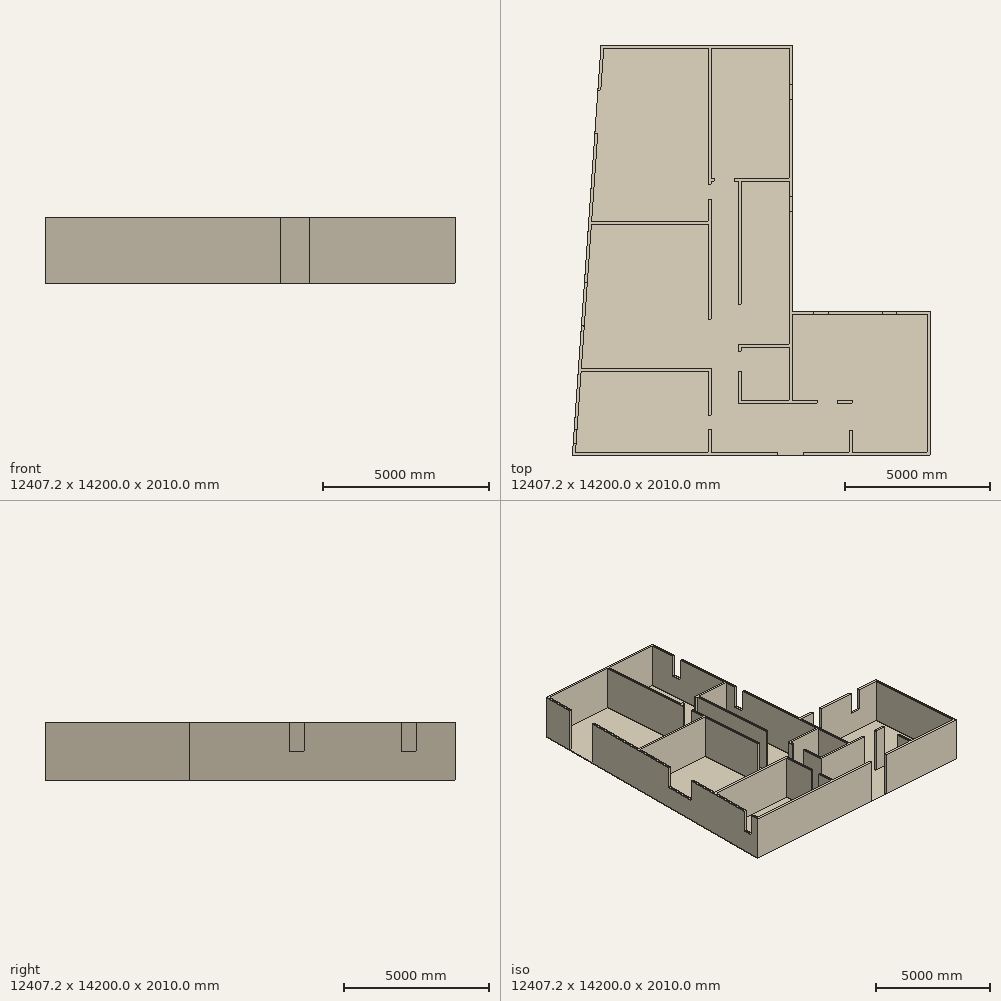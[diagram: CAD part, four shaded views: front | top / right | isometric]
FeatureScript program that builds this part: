
annotation { "Feature Type Name" : "Feature", "Feature Type Description" : "" }
export const myFeature = defineFeature(function(context is Context, id is Id, definition is map)
    precondition{}
    {
        {
            var Q0;
            Q0=qCreatedBy(makeId("Top.planeOp"),FACE);
            var sketch = newSketch(context, id + "F0", { "sketchPlane" : qUnion([Q0])});
            skLineSegment(sketch, "E0.bottom", {"start": v(0, 0) * mm, "end": v(20000, 0) * mm, "construction": true});
            skLineSegment(sketch, "E0.top", {"start": v(0, 20000) * mm, "end": v(20000, 20000) * mm, "construction": true});
            skLineSegment(sketch, "E0.left", {"start": v(0, 0) * mm, "end": v(0, 20000) * mm, "construction": true});
            skLineSegment(sketch, "E0.right", {"start": v(20000, 0) * mm, "end": v(20000, 20000) * mm, "construction": true});
            skLineSegment(sketch, "E1.bottom", {"start": v(0, 0) * mm, "end": v(100, 0) * mm, "construction": true});
            skLineSegment(sketch, "E1.top", {"start": v(0, 100) * mm, "end": v(100, 100) * mm, "construction": true});
            skLineSegment(sketch, "E1.left", {"start": v(0, 0) * mm, "end": v(0, 100) * mm, "construction": true});
            skLineSegment(sketch, "E1.right", {"start": v(100, 0) * mm, "end": v(100, 100) * mm, "construction": true});
            skLineSegment(sketch, "E2", {"start": v(100, 100) * mm, "end": v(1078.98, 14100) * mm});
            skLineSegment(sketch, "E3", {"start": v(100, 100) * mm, "end": v(12300, 100) * mm});
            skLineSegment(sketch, "E4", {"start": v(12300, 100) * mm, "end": v(12300, 4900) * mm});
            skLineSegment(sketch, "E5", {"start": v(7500, 4900) * mm, "end": v(7500, 14100) * mm});
            skLineSegment(sketch, "E6", {"start": v(1078.98, 14100) * mm, "end": v(4209.58, 14100) * mm});
            skLineSegment(sketch, "E7", {"start": v(4209.58, 14100) * mm, "end": v(7500, 14100) * mm});
            skLineSegment(sketch, "E8", {"start": v(7500, 4900) * mm, "end": v(12300, 4900) * mm});
            skSolve(sketch);
        }
        {
            var Q0;
            Q0=qCreatedBy(makeId("Top.planeOp"),FACE);
            var sketch = newSketch(context, id + "F1", { "sketchPlane" : qUnion([Q0])});
            skLineSegment(sketch, "E9.0", {"start": v(985.72, 14200) * mm, "end": v(4226.15, 14200) * mm});
            skLineSegment(sketch, "E9.1", {"start": v(-7.24, 0) * mm, "end": v(985.72, 14200) * mm});
            skLineSegment(sketch, "E9.2", {"start": v(7600, 5000) * mm, "end": v(7600, 14200) * mm});
            skLineSegment(sketch, "E9.3", {"start": v(7600, 5000) * mm, "end": v(12400, 5000) * mm});
            skLineSegment(sketch, "E9.4", {"start": v(12400, 0) * mm, "end": v(12400, 5000) * mm});
            skLineSegment(sketch, "E9.5", {"start": v(4226.15, 14200) * mm, "end": v(7600, 14200) * mm});
            skLineSegment(sketch, "E9.6", {"start": v(-7.24, 0) * mm, "end": v(12400, 0) * mm});
            skLineSegment(sketch, "E10.0", {"start": v(1078.98, 14100) * mm, "end": v(4209.58, 14100) * mm});
            skLineSegment(sketch, "E10.1", {"start": v(100, 100) * mm, "end": v(1078.98, 14100) * mm});
            skLineSegment(sketch, "E10.2", {"start": v(7500, 4900) * mm, "end": v(7500, 14100) * mm});
            skLineSegment(sketch, "E10.3", {"start": v(7500, 4900) * mm, "end": v(12300, 4900) * mm});
            skLineSegment(sketch, "E10.4", {"start": v(12300, 100) * mm, "end": v(12300, 4900) * mm});
            skLineSegment(sketch, "E10.5", {"start": v(4209.58, 14100) * mm, "end": v(7500, 14100) * mm});
            skLineSegment(sketch, "E10.6", {"start": v(100, 100) * mm, "end": v(12300, 100) * mm});
            skLineSegment(sketch, "E11", {"start": v(7096.77, 100) * mm, "end": v(7096.77, 0) * mm});
            skLineSegment(sketch, "E12", {"start": v(7996.77, 0) * mm, "end": v(7996.77, 100) * mm});
            skLineSegment(sketch, "E13", {"start": v(8348.52, 5000) * mm, "end": v(8348.52, 4900) * mm});
            skLineSegment(sketch, "E14", {"start": v(8848.52, 4900) * mm, "end": v(8848.52, 5000) * mm});
            skLineSegment(sketch, "E15", {"start": v(10721.84, 4900) * mm, "end": v(10721.84, 5000) * mm});
            skLineSegment(sketch, "E16", {"start": v(11221.84, 4900) * mm, "end": v(11221.84, 5000) * mm});
            skLineSegment(sketch, "E17", {"start": v(21.17, 406.24) * mm, "end": v(120.93, 399.27) * mm});
            skLineSegment(sketch, "E18", {"start": v(56.05, 905.03) * mm, "end": v(155.8, 898.05) * mm});
            skLineSegment(sketch, "E19", {"start": v(306.67, 4489.04) * mm, "end": v(406.42, 4482.06) * mm});
            skLineSegment(sketch, "E20", {"start": v(411.3, 5985.38) * mm, "end": v(511.06, 5978.4) * mm});
            skLineSegment(sketch, "E21", {"start": v(771.9, 11142.25) * mm, "end": v(871.66, 11135.28) * mm});
            skLineSegment(sketch, "E22", {"start": v(876.54, 12638.6) * mm, "end": v(976.3, 12631.63) * mm});
            skLineSegment(sketch, "E23", {"start": v(7500, 12837.72) * mm, "end": v(7600, 12837.72) * mm});
            skLineSegment(sketch, "E24", {"start": v(7500, 12337.72) * mm, "end": v(7600, 12337.72) * mm});
            skLineSegment(sketch, "E25", {"start": v(7600, 8958.3) * mm, "end": v(7500, 8958.3) * mm});
            skLineSegment(sketch, "E26", {"start": v(7600, 8458.3) * mm, "end": v(7500, 8458.3) * mm});
            skSolve(sketch);
        }
        {
            var Q0;
            Q0=qCreatedBy(makeId("Top.planeOp"),FACE);
            var sketch = newSketch(context, id + "F2", { "sketchPlane" : qUnion([Q0])});
            skPoint(sketch, "E27", {"position": v(12300, 100) * mm});
            skPoint(sketch, "E28", {"position": v(100, 100) * mm});
            skPoint(sketch, "E29", {"position": v(12300, 4900) * mm});
            skPoint(sketch, "E30", {"position": v(7500, 4900) * mm});
            skPoint(sketch, "E31", {"position": v(7500, 14100) * mm});
            skPoint(sketch, "E32", {"position": v(1078.98, 14100) * mm});
            skPoint(sketch, "E33", {"position": v(4209.58, 14100) * mm});
            skLineSegment(sketch, "E34.bottom", {"start": v(9600, 100) * mm, "end": v(9700, 100) * mm});
            skLineSegment(sketch, "E34.top", {"start": v(9600, 881.62) * mm, "end": v(9700, 881.62) * mm});
            skLineSegment(sketch, "E34.left", {"start": v(9700, 100) * mm, "end": v(9700, 881.62) * mm});
            skLineSegment(sketch, "E34.right", {"start": v(9600, 100) * mm, "end": v(9600, 881.62) * mm});
            skLineSegment(sketch, "E35.top", {"start": v(302.79, 3000) * mm, "end": v(4800, 3000) * mm});
            skLineSegment(sketch, "E35.right", {"start": v(4800, 2900) * mm, "end": v(4800, 3000) * mm});
            skLineSegment(sketch, "E36", {"start": v(4800, 2900) * mm, "end": v(295.8, 2900) * mm});
            skLineSegment(sketch, "E37", {"start": v(295.8, 2900) * mm, "end": v(302.79, 3000) * mm});
            skLineSegment(sketch, "E38.bottom", {"start": v(7500, 4900) * mm, "end": v(7600, 4900) * mm});
            skLineSegment(sketch, "E38.top", {"start": v(7500, 1800) * mm, "end": v(7600, 1800) * mm});
            skLineSegment(sketch, "E38.left", {"start": v(7500, 4900) * mm, "end": v(7500, 1800) * mm});
            skLineSegment(sketch, "E38.right", {"start": v(7600, 4900) * mm, "end": v(7600, 1800) * mm});
            skLineSegment(sketch, "E39.bottom", {"start": v(7600, 1800) * mm, "end": v(8479.6, 1800) * mm});
            skLineSegment(sketch, "E39.top", {"start": v(7600, 1900) * mm, "end": v(8479.6, 1900) * mm});
            skLineSegment(sketch, "E39.left", {"start": v(7600, 1800) * mm, "end": v(7600, 1900) * mm});
            skLineSegment(sketch, "E39.right", {"start": v(8479.6, 1800) * mm, "end": v(8479.6, 1900) * mm});
            skLineSegment(sketch, "E40.bottom", {"start": v(9179.6, 1800) * mm, "end": v(9700, 1800) * mm});
            skLineSegment(sketch, "E40.top", {"start": v(9179.6, 1900) * mm, "end": v(9700, 1900) * mm});
            skLineSegment(sketch, "E40.left", {"start": v(9179.6, 1800) * mm, "end": v(9179.6, 1900) * mm});
            skLineSegment(sketch, "E40.right", {"start": v(9700, 1800) * mm, "end": v(9700, 1900) * mm});
            skLineSegment(sketch, "E41.bottom", {"start": v(9700, 1900) * mm, "end": v(9600, 1900) * mm});
            skLineSegment(sketch, "E41.top", {"start": v(9700, 4900) * mm, "end": v(9600, 4900) * mm});
            skLineSegment(sketch, "E41.left", {"start": v(9700, 1900) * mm, "end": v(9700, 4900) * mm});
            skLineSegment(sketch, "E41.right", {"start": v(9600, 1900) * mm, "end": v(9600, 4900) * mm});
            skLineSegment(sketch, "E42.bottom", {"start": v(7500, 1800) * mm, "end": v(5840, 1800) * mm});
            skLineSegment(sketch, "E42.top", {"start": v(7500, 1900) * mm, "end": v(5840, 1900) * mm});
            skLineSegment(sketch, "E42.left", {"start": v(7500, 1800) * mm, "end": v(7500, 1900) * mm});
            skLineSegment(sketch, "E42.right", {"start": v(5840, 1800) * mm, "end": v(5840, 1900) * mm});
            skLineSegment(sketch, "E43", {"start": v(659.41, 8100) * mm, "end": v(652.42, 8000) * mm});
            skLineSegment(sketch, "E44", {"start": v(9700, 490.8) * mm, "end": v(12300, 490.8) * mm});
            skLineSegment(sketch, "E45.bottom", {"start": v(9700, 1800) * mm, "end": v(9600, 1800) * mm});
            skLineSegment(sketch, "E45.top", {"start": v(9700, 1581.62) * mm, "end": v(9600, 1581.62) * mm});
            skLineSegment(sketch, "E45.left", {"start": v(9700, 1800) * mm, "end": v(9700, 1581.62) * mm});
            skLineSegment(sketch, "E45.right", {"start": v(9600, 1800) * mm, "end": v(9600, 1581.62) * mm});
            skPoint(sketch, "E46", {"position": v(4750, 100) * mm});
            skLineSegment(sketch, "E47.bottom", {"start": v(4700, 900.8) * mm, "end": v(4800, 900.8) * mm});
            skLineSegment(sketch, "E47.top", {"start": v(4700, 100) * mm, "end": v(4800, 100) * mm});
            skLineSegment(sketch, "E47.left", {"start": v(4700, 900.8) * mm, "end": v(4700, 100) * mm});
            skLineSegment(sketch, "E47.right", {"start": v(4800, 900.8) * mm, "end": v(4800, 100) * mm});
            skLineSegment(sketch, "E48.bottom", {"start": v(4700, 1375.58) * mm, "end": v(4800, 1375.58) * mm});
            skLineSegment(sketch, "E48.top", {"start": v(4700, 2900) * mm, "end": v(4800, 2900) * mm});
            skLineSegment(sketch, "E48.left", {"start": v(4700, 1375.58) * mm, "end": v(4700, 2900) * mm});
            skLineSegment(sketch, "E48.right", {"start": v(4800, 1375.58) * mm, "end": v(4800, 2900) * mm});
            skLineSegment(sketch, "E49.bottom", {"start": v(5840, 1800) * mm, "end": v(5740, 1800) * mm});
            skLineSegment(sketch, "E49.top", {"start": v(5840, 2896.25) * mm, "end": v(5740, 2896.25) * mm});
            skLineSegment(sketch, "E49.left", {"start": v(5840, 1800) * mm, "end": v(5840, 2896.25) * mm});
            skLineSegment(sketch, "E49.right", {"start": v(5740, 1800) * mm, "end": v(5740, 2896.25) * mm});
            skLineSegment(sketch, "E50.bottom", {"start": v(5740, 3750) * mm, "end": v(5840, 3750) * mm});
            skLineSegment(sketch, "E50.top", {"start": v(5740, 3596.25) * mm, "end": v(5840, 3596.25) * mm});
            skLineSegment(sketch, "E50.left", {"start": v(5740, 3750) * mm, "end": v(5740, 3596.25) * mm});
            skLineSegment(sketch, "E50.right", {"start": v(5840, 3750) * mm, "end": v(5840, 3596.25) * mm});
            skLineSegment(sketch, "E51.bottom", {"start": v(5740, 3750) * mm, "end": v(7500, 3750) * mm});
            skLineSegment(sketch, "E51.top", {"start": v(5740, 3850) * mm, "end": v(7500, 3850) * mm});
            skLineSegment(sketch, "E51.left", {"start": v(5740, 3750) * mm, "end": v(5740, 3850) * mm});
            skLineSegment(sketch, "E51.right", {"start": v(7500, 3750) * mm, "end": v(7500, 3850) * mm});
            skLineSegment(sketch, "E52.bottom", {"start": v(5740, 3850) * mm, "end": v(5840, 3850) * mm});
            skLineSegment(sketch, "E52.top", {"start": v(5740, 4524.1) * mm, "end": v(5840, 4524.1) * mm});
            skLineSegment(sketch, "E52.left", {"start": v(5740, 3850) * mm, "end": v(5740, 4524.1) * mm});
            skLineSegment(sketch, "E52.right", {"start": v(5840, 3850) * mm, "end": v(5840, 4524.1) * mm});
            skLineSegment(sketch, "E53.bottom", {"start": v(5740, 9500) * mm, "end": v(5840, 9500) * mm});
            skLineSegment(sketch, "E53.top", {"start": v(5740, 5224.1) * mm, "end": v(5840, 5224.1) * mm});
            skLineSegment(sketch, "E53.left", {"start": v(5740, 9500) * mm, "end": v(5740, 5224.1) * mm});
            skLineSegment(sketch, "E53.right", {"start": v(5840, 9500) * mm, "end": v(5840, 5224.1) * mm});
            skLineSegment(sketch, "E54.bottom", {"start": v(5740, 9500) * mm, "end": v(7500, 9500) * mm});
            skLineSegment(sketch, "E54.top", {"start": v(5740, 9600) * mm, "end": v(7500, 9600) * mm});
            skLineSegment(sketch, "E54.left", {"start": v(5740, 9500) * mm, "end": v(5740, 9600) * mm});
            skLineSegment(sketch, "E54.right", {"start": v(7500, 9500) * mm, "end": v(7500, 9600) * mm});
            skLineSegment(sketch, "E55", {"start": v(659.41, 8100) * mm, "end": v(4700, 8100) * mm});
            skLineSegment(sketch, "E56", {"start": v(4700, 8100) * mm, "end": v(4700, 8000) * mm});
            skLineSegment(sketch, "E57", {"start": v(4700, 8000) * mm, "end": v(652.42, 8000) * mm});
            skLineSegment(sketch, "E58.bottom", {"start": v(4800, 3000) * mm, "end": v(4700, 3000) * mm});
            skLineSegment(sketch, "E58.top", {"start": v(4800, 3303.02) * mm, "end": v(4700, 3303.02) * mm});
            skLineSegment(sketch, "E58.left", {"start": v(4800, 3000) * mm, "end": v(4800, 3303.02) * mm});
            skLineSegment(sketch, "E58.right", {"start": v(4700, 3000) * mm, "end": v(4700, 3303.02) * mm});
            skLineSegment(sketch, "E59.bottom", {"start": v(4700, 4703.02) * mm, "end": v(4800, 4703.02) * mm});
            skLineSegment(sketch, "E59.top", {"start": v(4700, 8854.76) * mm, "end": v(4800, 8854.76) * mm});
            skLineSegment(sketch, "E59.left", {"start": v(4700, 4703.02) * mm, "end": v(4700, 8854.76) * mm});
            skLineSegment(sketch, "E59.right", {"start": v(4800, 4703.02) * mm, "end": v(4800, 8854.76) * mm});
            skLineSegment(sketch, "E60.bottom", {"start": v(4800, 9381.01) * mm, "end": v(4700, 9381.01) * mm});
            skLineSegment(sketch, "E60.top", {"start": v(4800, 14100) * mm, "end": v(4700, 14100) * mm});
            skLineSegment(sketch, "E60.left", {"start": v(4800, 9381.01) * mm, "end": v(4800, 14100) * mm});
            skLineSegment(sketch, "E60.right", {"start": v(4700, 9381.01) * mm, "end": v(4700, 14100) * mm});
            skLineSegment(sketch, "E61.bottom", {"start": v(4800, 9500) * mm, "end": v(4905.82, 9500) * mm});
            skLineSegment(sketch, "E61.top", {"start": v(4800, 9600) * mm, "end": v(4905.82, 9600) * mm});
            skLineSegment(sketch, "E61.left", {"start": v(4800, 9500) * mm, "end": v(4800, 9600) * mm});
            skLineSegment(sketch, "E61.right", {"start": v(4905.82, 9500) * mm, "end": v(4905.82, 9600) * mm});
            skLineSegment(sketch, "E62.bottom", {"start": v(5605.82, 9600) * mm, "end": v(5740, 9600) * mm});
            skLineSegment(sketch, "E62.top", {"start": v(5605.82, 9500) * mm, "end": v(5740, 9500) * mm});
            skLineSegment(sketch, "E62.left", {"start": v(5605.82, 9600) * mm, "end": v(5605.82, 9500) * mm});
            skLineSegment(sketch, "E62.right", {"start": v(5740, 9600) * mm, "end": v(5740, 9500) * mm});
            skLineSegment(sketch, "E63", {"start": v(13077.34, 3850) * mm, "end": v(13077.34, 6950) * mm});
            skSolve(sketch);
        }
        {
            var Q0;
            {var subQ23=sQuery(id+"F1.wireOp",EDGE,"E10.0");Q0=makeQuery(id+"F1.imprint","IMPRINT",FACE,{"disambiguationData":[TD([[makeQuery(id+"F1.imprint","IMPRINT",EDGE,{"derivedFrom":subQ23}),-1.0]])]});}
            var Q1;
            {var subQ0=sQuery(id+"F1.wireOp",EDGE,"E20");Q1=makeQuery(id+"F1.imprint","IMPRINT",FACE,{"disambiguationData":[TD([[makeQuery(id+"F1.imprint","IMPRINT",EDGE,{"derivedFrom":subQ0}),1.0]])]});}
            var Q2;
            {var subQ2=sQuery(id+"F1.wireOp",EDGE,"E9.0");Q2=makeQuery(id+"F1.imprint","IMPRINT",FACE,{"disambiguationData":[TD([[makeQuery(id+"F1.imprint","IMPRINT",EDGE,{"derivedFrom":subQ2}),-1.0]])]});}
            var Q3;
            {var subQ0=sQuery(id+"F1.wireOp",EDGE,"E24");Q3=makeQuery(id+"F1.imprint","IMPRINT",FACE,{"disambiguationData":[TD([[makeQuery(id+"F1.imprint","IMPRINT",EDGE,{"derivedFrom":subQ0}),-1.0]])]});}
            var Q4;
            {var subQ3=sQuery(id+"F1.wireOp",EDGE,"E13");Q4=makeQuery(id+"F1.imprint","IMPRINT",FACE,{"disambiguationData":[TD([[makeQuery(id+"F1.imprint","IMPRINT",EDGE,{"derivedFrom":subQ3}),-1.0]])]});}
            var Q5;
            {var subQ0=sQuery(id+"F1.wireOp",EDGE,"E14");Q5=makeQuery(id+"F1.imprint","IMPRINT",FACE,{"disambiguationData":[TD([[makeQuery(id+"F1.imprint","IMPRINT",EDGE,{"derivedFrom":subQ0}),-1.0]])]});}
            var Q6;
            {var subQ1=sQuery(id+"F1.wireOp",EDGE,"E9.4");Q6=makeQuery(id+"F1.imprint","IMPRINT",FACE,{"disambiguationData":[TD([[makeQuery(id+"F1.imprint","IMPRINT",EDGE,{"derivedFrom":subQ1}),1.0]])]});}
            var Q7;
            {var subQ7=sQuery(id+"F1.wireOp",EDGE,"E11");Q7=makeQuery(id+"F1.imprint","IMPRINT",FACE,{"disambiguationData":[TD([[makeQuery(id+"F1.imprint","IMPRINT",EDGE,{"derivedFrom":subQ7}),-1.0]])]});}
            var Q8;
            {var subQ0=sQuery(id+"F1.wireOp",EDGE,"E18");Q8=makeQuery(id+"F1.imprint","IMPRINT",FACE,{"disambiguationData":[TD([[makeQuery(id+"F1.imprint","IMPRINT",EDGE,{"derivedFrom":subQ0}),1.0]])]});}
            var Q9;
            {var subQ0=sQuery(id+"F1.wireOp",EDGE,"E25");Q9=makeQuery(id+"F1.imprint","IMPRINT",FACE,{"disambiguationData":[TD([[makeQuery(id+"F1.imprint","IMPRINT",EDGE,{"derivedFrom":subQ0}),1.0]])]});}
            var Q10;
            {var subQ0=sQuery(id+"F1.wireOp",EDGE,"E23");Q10=makeQuery(id+"F1.imprint","IMPRINT",FACE,{"disambiguationData":[TD([[makeQuery(id+"F1.imprint","IMPRINT",EDGE,{"derivedFrom":subQ0}),-1.0]])]});}
            var Q11;
            {var subQ0=sQuery(id+"F1.wireOp",EDGE,"E15");Q11=makeQuery(id+"F1.imprint","IMPRINT",FACE,{"disambiguationData":[TD([[makeQuery(id+"F1.imprint","IMPRINT",EDGE,{"derivedFrom":subQ0}),-1.0]])]});}
            var Q12;
            {var subQ0=sQuery(id+"F1.wireOp",EDGE,"E13");Q12=makeQuery(id+"F1.imprint","IMPRINT",FACE,{"disambiguationData":[TD([[makeQuery(id+"F1.imprint","IMPRINT",EDGE,{"derivedFrom":subQ0}),1.0]])]});}
            var Q13;
            {var subQ0=sQuery(id+"F1.wireOp",EDGE,"E19");Q13=makeQuery(id+"F1.imprint","IMPRINT",FACE,{"disambiguationData":[TD([[makeQuery(id+"F1.imprint","IMPRINT",EDGE,{"derivedFrom":subQ0}),1.0]])]});}
            var Q14;
            {var subQ0=sQuery(id+"F1.wireOp",EDGE,"E17");Q14=makeQuery(id+"F1.imprint","IMPRINT",FACE,{"disambiguationData":[TD([[makeQuery(id+"F1.imprint","IMPRINT",EDGE,{"derivedFrom":subQ0}),1.0]])]});}
            var Q15;
            {var subQ0=sQuery(id+"F1.wireOp",EDGE,"E11");Q15=makeQuery(id+"F1.imprint","IMPRINT",FACE,{"disambiguationData":[TD([[makeQuery(id+"F1.imprint","IMPRINT",EDGE,{"derivedFrom":subQ0}),1.0]])]});}
            var Q16;
            {var subQ0=sQuery(id+"F1.wireOp",EDGE,"E21");Q16=makeQuery(id+"F1.imprint","IMPRINT",FACE,{"disambiguationData":[TD([[makeQuery(id+"F1.imprint","IMPRINT",EDGE,{"derivedFrom":subQ0}),1.0]])]});}
            extrude(context, id + "F3", {"entities" : qUnion([Q0, Q1, Q2, Q3, Q4, Q5, Q6, Q7, Q8, Q9, Q10, Q11, Q12, Q13, Q14, Q15, Q16]), "oppositeDirection" : true, "depth" : 10 * mm});
        }
        {
            var Q0;
            {var subQ0=sQuery(id+"F1.wireOp",EDGE,"E24");Q0=makeQuery(id+"F1.imprint","IMPRINT",FACE,{"disambiguationData":[TD([[makeQuery(id+"F1.imprint","IMPRINT",EDGE,{"derivedFrom":subQ0}),-1.0]])]});}
            var Q1;
            {var subQ3=sQuery(id+"F1.wireOp",EDGE,"E13");Q1=makeQuery(id+"F1.imprint","IMPRINT",FACE,{"disambiguationData":[TD([[makeQuery(id+"F1.imprint","IMPRINT",EDGE,{"derivedFrom":subQ3}),-1.0]])]});}
            var Q2;
            {var subQ0=sQuery(id+"F1.wireOp",EDGE,"E20");Q2=makeQuery(id+"F1.imprint","IMPRINT",FACE,{"disambiguationData":[TD([[makeQuery(id+"F1.imprint","IMPRINT",EDGE,{"derivedFrom":subQ0}),1.0]])]});}
            var Q3;
            {var subQ0=sQuery(id+"F1.wireOp",EDGE,"E18");Q3=makeQuery(id+"F1.imprint","IMPRINT",FACE,{"disambiguationData":[TD([[makeQuery(id+"F1.imprint","IMPRINT",EDGE,{"derivedFrom":subQ0}),1.0]])]});}
            var Q4;
            {var subQ7=sQuery(id+"F1.wireOp",EDGE,"E11");Q4=makeQuery(id+"F1.imprint","IMPRINT",FACE,{"disambiguationData":[TD([[makeQuery(id+"F1.imprint","IMPRINT",EDGE,{"derivedFrom":subQ7}),-1.0]])]});}
            var Q5;
            {var subQ1=sQuery(id+"F1.wireOp",EDGE,"E9.4");Q5=makeQuery(id+"F1.imprint","IMPRINT",FACE,{"disambiguationData":[TD([[makeQuery(id+"F1.imprint","IMPRINT",EDGE,{"derivedFrom":subQ1}),1.0]])]});}
            var Q6;
            {var subQ0=sQuery(id+"F1.wireOp",EDGE,"E14");Q6=makeQuery(id+"F1.imprint","IMPRINT",FACE,{"disambiguationData":[TD([[makeQuery(id+"F1.imprint","IMPRINT",EDGE,{"derivedFrom":subQ0}),-1.0]])]});}
            var Q7;
            {var subQ2=sQuery(id+"F1.wireOp",EDGE,"E9.0");Q7=makeQuery(id+"F1.imprint","IMPRINT",FACE,{"disambiguationData":[TD([[makeQuery(id+"F1.imprint","IMPRINT",EDGE,{"derivedFrom":subQ2}),-1.0]])]});}
            extrude(context, id + "F4", {"entities" : qUnion([Q0, Q1, Q2, Q3, Q4, Q5, Q6, Q7]), "operationType" : NewBodyOperationType.ADD, "depth" : 2000 * mm});
        }
        {
            var Q0;
            Q0=makeQuery(id+"F2.imprint","IMPRINT",FACE,{"disambiguationData":[TD([[makeQuery(id+"F2.imprint","IMPRINT",EDGE,{"derivedFrom":sQuery(id+"F2.wireOp",EDGE,"E43")}),1.0]])]});
            var Q1;
            {var subQ3=sQuery(id+"F2.wireOp",EDGE,"E60.bottom");Q1=makeQuery(id+"F2.imprint","IMPRINT",FACE,{"disambiguationData":[TD([[makeQuery(id+"F2.imprint","IMPRINT",EDGE,{"derivedFrom":subQ3}),-1.0]])]});}
            var Q2;
            Q2=makeQuery(id+"F2.imprint","IMPRINT",FACE,{"disambiguationData":[TD([[makeQuery(id+"F2.imprint","IMPRINT",EDGE,{"derivedFrom":sQuery(id+"F2.wireOp",EDGE,"E61.bottom")}),1.0]])]});
            var Q3;
            Q3=makeQuery(id+"F2.imprint","IMPRINT",FACE,{"disambiguationData":[TD([[makeQuery(id+"F2.imprint","IMPRINT",EDGE,{"derivedFrom":sQuery(id+"F2.wireOp",EDGE,"E54.top")}),-1.0]])]});
            var Q4;
            Q4=makeQuery(id+"F2.imprint","IMPRINT",FACE,{"disambiguationData":[TD([[makeQuery(id+"F2.imprint","IMPRINT",EDGE,{"derivedFrom":sQuery(id+"F2.wireOp",EDGE,"E62.bottom")}),-1.0]])]});
            var Q5;
            Q5=makeQuery(id+"F2.imprint","IMPRINT",FACE,{"disambiguationData":[TD([[makeQuery(id+"F2.imprint","IMPRINT",EDGE,{"derivedFrom":sQuery(id+"F2.wireOp",EDGE,"E53.top")}),1.0]])]});
            var Q6;
            Q6=makeQuery(id+"F2.imprint","IMPRINT",FACE,{"disambiguationData":[TD([[makeQuery(id+"F2.imprint","IMPRINT",EDGE,{"derivedFrom":sQuery(id+"F2.wireOp",EDGE,"E35.top")}),-1.0]])]});
            var Q7;
            Q7=makeQuery(id+"F2.imprint","IMPRINT",FACE,{"disambiguationData":[TD([[makeQuery(id+"F2.imprint","IMPRINT",EDGE,{"derivedFrom":sQuery(id+"F2.wireOp",EDGE,"E58.bottom")}),-1.0]])]});
            var Q8;
            Q8=makeQuery(id+"F2.imprint","IMPRINT",FACE,{"disambiguationData":[TD([[makeQuery(id+"F2.imprint","IMPRINT",EDGE,{"derivedFrom":sQuery(id+"F2.wireOp",EDGE,"E48.bottom")}),1.0]])]});
            var Q9;
            {var subQ3=sQuery(id+"F2.wireOp",EDGE,"E59.bottom");Q9=makeQuery(id+"F2.imprint","IMPRINT",FACE,{"disambiguationData":[TD([[makeQuery(id+"F2.imprint","IMPRINT",EDGE,{"derivedFrom":subQ3}),1.0]])]});}
            var Q10;
            Q10=makeQuery(id+"F2.imprint","IMPRINT",FACE,{"disambiguationData":[TD([[makeQuery(id+"F2.imprint","IMPRINT",EDGE,{"derivedFrom":sQuery(id+"F2.wireOp",EDGE,"E52.bottom")}),1.0]])]});
            var Q11;
            Q11=makeQuery(id+"F2.imprint","IMPRINT",FACE,{"disambiguationData":[TD([[makeQuery(id+"F2.imprint","IMPRINT",EDGE,{"derivedFrom":sQuery(id+"F2.wireOp",EDGE,"E51.top")}),-1.0]])]});
            var Q12;
            Q12=makeQuery(id+"F2.imprint","IMPRINT",FACE,{"disambiguationData":[TD([[makeQuery(id+"F2.imprint","IMPRINT",EDGE,{"derivedFrom":sQuery(id+"F2.wireOp",EDGE,"E50.top")}),1.0]])]});
            var Q13;
            {var subQ3=sQuery(id+"F2.wireOp",EDGE,"E49.bottom");Q13=makeQuery(id+"F2.imprint","IMPRINT",FACE,{"disambiguationData":[TD([[makeQuery(id+"F2.imprint","IMPRINT",EDGE,{"derivedFrom":subQ3}),-1.0]])]});}
            var Q14;
            {var subQ0=sQuery(id+"F2.wireOp",EDGE,"E42.bottom");Q14=makeQuery(id+"F2.imprint","IMPRINT",FACE,{"disambiguationData":[TD([[makeQuery(id+"F2.imprint","IMPRINT",EDGE,{"derivedFrom":subQ0}),-1.0]])]});}
            var Q15;
            {var subQ1=sQuery(id+"F2.wireOp",EDGE,"E38.bottom");Q15=makeQuery(id+"F2.imprint","IMPRINT",FACE,{"disambiguationData":[TD([[makeQuery(id+"F2.imprint","IMPRINT",EDGE,{"derivedFrom":subQ1}),-1.0]])]});}
            var Q16;
            Q16=makeQuery(id+"F2.imprint","IMPRINT",FACE,{"disambiguationData":[TD([[makeQuery(id+"F2.imprint","IMPRINT",EDGE,{"derivedFrom":sQuery(id+"F2.wireOp",EDGE,"E39.bottom")}),1.0]])]});
            var Q17;
            Q17=makeQuery(id+"F2.imprint","IMPRINT",FACE,{"disambiguationData":[TD([[makeQuery(id+"F2.imprint","IMPRINT",EDGE,{"derivedFrom":sQuery(id+"F2.wireOp",EDGE,"E47.bottom")}),-1.0]])]});
            var Q18;
            Q18=makeQuery(id+"F2.imprint","IMPRINT",FACE,{"disambiguationData":[TD([[makeQuery(id+"F2.imprint","IMPRINT",EDGE,{"derivedFrom":sQuery(id+"F2.wireOp",EDGE,"E41.bottom")}),-1.0]])]});
            var Q19;
            Q19=makeQuery(id+"F2.imprint","IMPRINT",FACE,{"disambiguationData":[TD([[makeQuery(id+"F2.imprint","IMPRINT",EDGE,{"derivedFrom":sQuery(id+"F2.wireOp",EDGE,"E40.bottom")}),1.0]])]});
            var Q20;
            Q20=makeQuery(id+"F2.imprint","IMPRINT",FACE,{"disambiguationData":[TD([[makeQuery(id+"F2.imprint","IMPRINT",EDGE,{"derivedFrom":sQuery(id+"F2.wireOp",EDGE,"E45.bottom")}),1.0]])]});
            var Q21;
            {var subQ3=sQuery(id+"F2.wireOp",EDGE,"E34.bottom");Q21=makeQuery(id+"F2.imprint","IMPRINT",FACE,{"disambiguationData":[TD([[makeQuery(id+"F2.imprint","IMPRINT",EDGE,{"derivedFrom":subQ3}),1.0]])]});}
            extrude(context, id + "F5", {"entities" : qUnion([Q0, Q1, Q2, Q3, Q4, Q5, Q6, Q7, Q8, Q9, Q10, Q11, Q12, Q13, Q14, Q15, Q16, Q17, Q18, Q19, Q20, Q21]), "operationType" : NewBodyOperationType.ADD, "depth" : 2000 * mm});
        }
        {
            var Q0;
            {var subQ0=sQuery(id+"F1.wireOp",EDGE,"E19");Q0=makeQuery(id+"F1.imprint","IMPRINT",FACE,{"disambiguationData":[TD([[makeQuery(id+"F1.imprint","IMPRINT",EDGE,{"derivedFrom":subQ0}),1.0]])]});}
            var Q1;
            {var subQ0=sQuery(id+"F1.wireOp",EDGE,"E17");Q1=makeQuery(id+"F1.imprint","IMPRINT",FACE,{"disambiguationData":[TD([[makeQuery(id+"F1.imprint","IMPRINT",EDGE,{"derivedFrom":subQ0}),1.0]])]});}
            var Q2;
            {var subQ0=sQuery(id+"F1.wireOp",EDGE,"E15");Q2=makeQuery(id+"F1.imprint","IMPRINT",FACE,{"disambiguationData":[TD([[makeQuery(id+"F1.imprint","IMPRINT",EDGE,{"derivedFrom":subQ0}),-1.0]])]});}
            var Q3;
            {var subQ0=sQuery(id+"F1.wireOp",EDGE,"E13");Q3=makeQuery(id+"F1.imprint","IMPRINT",FACE,{"disambiguationData":[TD([[makeQuery(id+"F1.imprint","IMPRINT",EDGE,{"derivedFrom":subQ0}),1.0]])]});}
            var Q4;
            {var subQ0=sQuery(id+"F1.wireOp",EDGE,"E25");Q4=makeQuery(id+"F1.imprint","IMPRINT",FACE,{"disambiguationData":[TD([[makeQuery(id+"F1.imprint","IMPRINT",EDGE,{"derivedFrom":subQ0}),1.0]])]});}
            var Q5;
            {var subQ0=sQuery(id+"F1.wireOp",EDGE,"E23");Q5=makeQuery(id+"F1.imprint","IMPRINT",FACE,{"disambiguationData":[TD([[makeQuery(id+"F1.imprint","IMPRINT",EDGE,{"derivedFrom":subQ0}),-1.0]])]});}
            extrude(context, id + "F6", {"entities" : qUnion([Q0, Q1, Q2, Q3, Q4, Q5]), "operationType" : NewBodyOperationType.ADD, "depth" : 1000 * mm});
        }
    });
